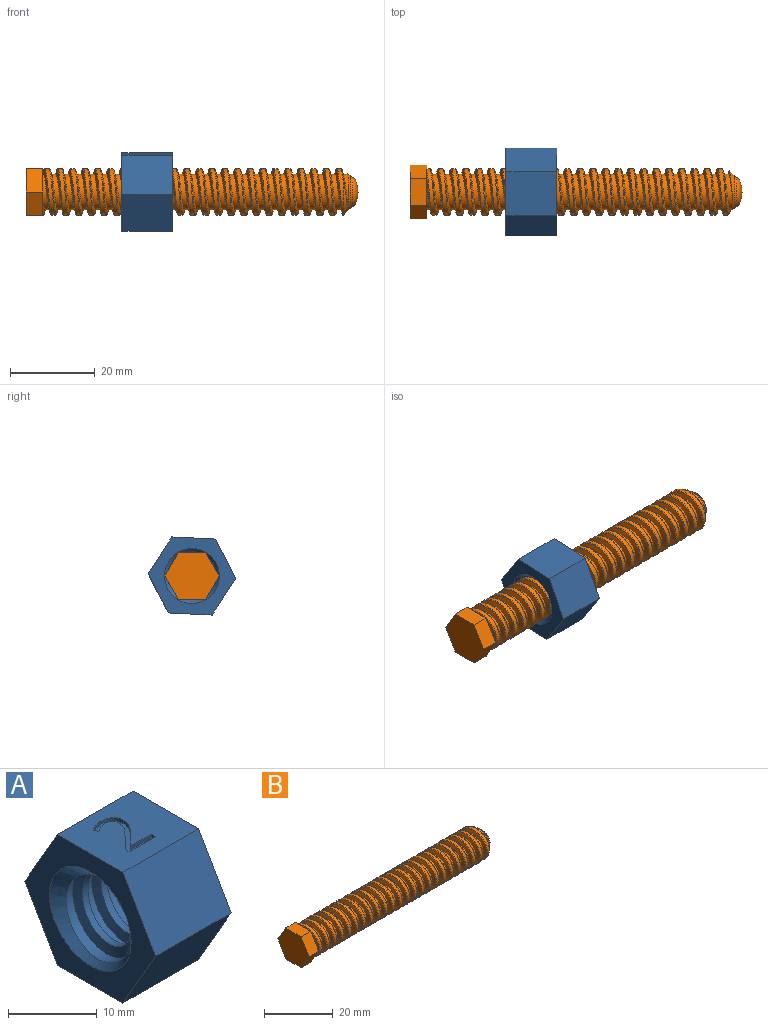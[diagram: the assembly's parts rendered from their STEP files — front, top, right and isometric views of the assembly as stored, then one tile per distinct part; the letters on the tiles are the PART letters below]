
ASSEMBLY  parts=2 mates=1
PART A: 35 faces, bbox 12.1x20.8x18 mm
  f0: plane 12x10.39mm, normal (0,0,1), area 115.7mm2, adj f3,f4,f7,f8,f14,f15,f16,f17
  f1: plane 12x10.39mm, normal (0,0,-1), area 124.7mm2, adj f2,f5,f7,f8
  f2: plane 12x9mm, normal (0,0.87,-0.5), area 124.7mm2, adj f1,f3,f7,f8
  f3: plane 12x9mm, normal (0,0.87,0.5), area 124.7mm2, adj f0,f2,f7,f8
  f4: plane 12x9mm, normal (0,-0.87,0.5), area 124.7mm2, adj f0,f5,f7,f8
  f5: plane 12x9mm, normal (0,-0.87,-0.5), area 124.7mm2, adj f1,f4,f7,f8
  f6: cylinder r=4.5mm len=9mm, axis (-1,0,0), area 69.4mm2, adj f9,f10,f12,f13
  f7: plane 20.78x18mm, normal (1,0,0), area 147.9mm2, adj f0,f1,f2,f3,f4,f5,f9
  f8: plane 20.78x18mm, normal (-1,0,0), area 147.9mm2, adj f0,f1,f2,f3,f4,f5,f10
  f9: cone r=4.5mm half-angle=45deg, axis (1,0,0), area 64.9mm2, adj f6,f7,f11,f12,f13
  f10: cone r=6.5mm half-angle=45deg, axis (-1,0,0), area 64.9mm2, adj f6,f8,f11,f12,f13
  f11: cylinder r=5.75mm len=11.5mm, axis (1,0,0), area 177.2mm2, adj f9,f10,f12,f13
  f12: bspline ~13.28x11.5mm, area 129.7mm2, adj f6,f9,f10,f11
  f13: bspline ~13.28x11.5mm, area 129.7mm2, adj f6,f9,f10,f11
  f14: plane 4.2x0.5mm, normal (0,1,0), area 2.1mm2, adj f0,f15,f33,f34
  f15: plane 0.67x0.5mm, normal (-1,0,0), area 0.3mm2, adj f0,f14,f16,f34
  f16: plane 3.29x0.5mm, normal (0,-1,0), area 1.6mm2, adj f0,f15,f17,f34
  f17: plane 0.5x0.04mm, normal (-1,0,0), area 0mm2, adj f0,f16,f18,f34
  f18: plane 1.4x1.37mm, normal (-0.7,0.71,0), area 1mm2, adj f0,f17,f19,f34
  f19: extruded ~1.5x1.28mm, area 1mm2, adj f0,f18,f20,f34
  f20: extruded ~1.2x0.5mm, area 0.6mm2, adj f0,f19,f21,f34
  f21: extruded ~1.24x0.51mm, area 0.7mm2, adj f0,f20,f22,f34
  f22: extruded ~1.41x0.5mm, area 0.8mm2, adj f0,f21,f23,f34
  f23: extruded ~1.92x0.73mm, area 1.1mm2, adj f0,f22,f24,f34
  f24: plane 0.5x0.49mm, normal (0.79,0.61,0), area 0.3mm2, adj f0,f23,f25,f34
  f25: extruded ~0.79x0.5mm, area 0.5mm2, adj f0,f24,f26,f34
  f26: extruded ~0.75x0.5mm, area 0.4mm2, adj f0,f25,f27,f34
  f27: extruded ~0.86x0.5mm, area 0.5mm2, adj f0,f26,f28,f34
  f28: extruded ~0.81x0.5mm, area 0.4mm2, adj f0,f27,f29,f34
  f29: extruded ~0.68x0.5mm, area 0.3mm2, adj f0,f28,f30,f34
  f30: extruded ~0.65x0.5mm, area 0.4mm2, adj f0,f29,f31,f34
  f31: extruded ~1.11x1.01mm, area 0.8mm2, adj f0,f30,f32,f34
  f32: plane 1.69x1.68mm, normal (0.71,-0.71,0), area 1.2mm2, adj f0,f31,f33,f34
  f33: plane 0.63x0.5mm, normal (1,0,0), area 0.3mm2, adj f0,f14,f32,f34
  f34: plane 6.48x4.2mm, normal (0,0,1), area 9mm2, adj f14,f15,f16,f17,f18,f19,f20,f21
PART B: 18 faces, bbox 78.7x12.9x11.2 mm
  f0: cylinder r=4.25mm len=72.25mm, axis (-1,0,0), area 1046.2mm2, adj f1,f2,f5,f12,f15
  f1: plane 0.2x0.16mm, normal (0,-1,0), area 0mm2, adj f0,f5,f15
  f2: bspline ~72.8x12.36mm, area 825.9mm2, adj f0,f3,f12,f15
  f3: bspline ~72.19x12.7mm, area 213mm2, adj f2,f12,f14,f15
  f4: bspline ~72.19x12.7mm, area 212.7mm2, adj f5,f12,f14,f15
  f5: bspline ~72.8x12.36mm, area 827.1mm2, adj f0,f1,f4,f12,f15
  f6: plane 6.35x4mm, normal (0,0,-1), area 25.4mm2, adj f7,f11,f12,f13
  f7: plane 5.5x4mm, normal (0,0.87,-0.5), area 25.4mm2, adj f6,f8,f12,f13
  f8: plane 5.5x4mm, normal (0,0.87,0.5), area 25.4mm2, adj f7,f9,f12,f13
  f9: plane 6.35x4mm, normal (0,0,1), area 25.4mm2, adj f8,f10,f12,f13
  f10: plane 5.5x4mm, normal (0,-0.87,0.5), area 25.4mm2, adj f9,f11,f12,f13
  f11: plane 5.5x4mm, normal (0,-0.87,-0.5), area 25.4mm2, adj f6,f10,f12,f13
  f12: plane 12.88x11.18mm, normal (1,0,0), area 28.3mm2, adj f0,f2,f3,f4,f5,f6,f7,f8
  f13: plane 12.7x11mm, normal (-1,0,0), area 104.8mm2, adj f6,f7,f8,f9,f10,f11
  f14: cylinder r=5.5mm len=71mm, axis (1,0,0), area 982.4mm2, adj f3,f4,f12,f15
  f15: cone r=3.5mm half-angle=45deg, axis (-1,0,0), area 41mm2, adj f0,f1,f2,f3,f4,f5,f14,f17
  f16: revolved ~6.89x6.89mm, area 44.2mm2, adj f17
  f17: torus R=5.29mm, axis (1,0,0), area 17.7mm2, adj f15,f16
PLACE A rot(axis=(0,-0.85,-0.52),180deg) t=(32.67,0,0)mm
PLACE B at identity fixed
MATE cylindrical A.f6 <-> B.f0  axis (-1,0,0) through (20.67,0,0)mm
